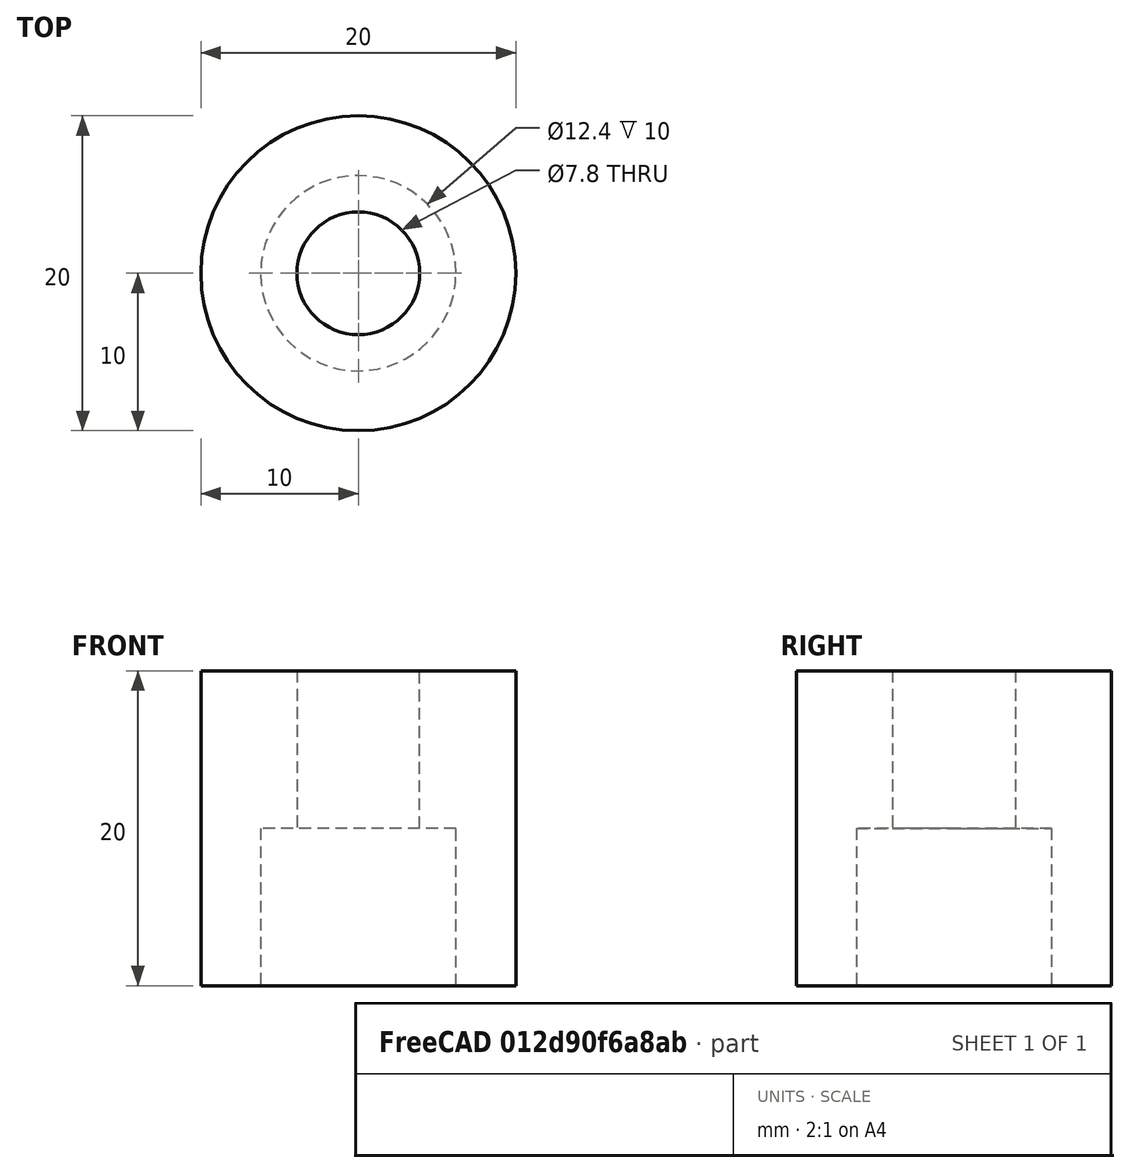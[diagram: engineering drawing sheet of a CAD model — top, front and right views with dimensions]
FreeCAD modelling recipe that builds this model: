
FCSTD DOCUMENT  (FreeCAD 1.0R38641 +468 (Git))
Label: m8_tube_extension
License: All rights reserved
LicenseURL: https://en.wikipedia.org/wiki/All_rights_reserved
objects: Sketcher::SketchObject×2, PartDesign::Pad×1, PartDesign::Pocket×1, PartDesign::Body×1
note: 11 computed .brp shape members not serialized (recipe doc carries the construction recipe); baked Part::Feature solids carry a one-line shape summary decoded from their .brp

FEATURE [Sketcher::SketchObject] Sketch
  ArcFitTolerance = 1e-06
  AttachmentSupport = -> [XY_Plane]
  FullyConstrained = false
  MakeInternals = false
  MapMode = 5
  sketch-geometry (2):
    g0: Circle CenterX=0 CenterY=0 CenterZ=0 NormalX=0 NormalY=0 NormalZ=1 AngleXU=0 Radius=10
    g1: Circle CenterX=0 CenterY=0 CenterZ=0 NormalX=0 NormalY=0 NormalZ=1 AngleXU=0 Radius=3.9
  constraints (3):
    c: Diameter(g0) = 20
    c: Diameter(g1) = 7.8
    c: Coincident(g1,g0)
FEATURE [PartDesign::Pad] Pad
  Direction = (0,0,1)
  Length = 20
  Length2 = 10
  Profile = -> Sketch
  ReferenceAxis = -> Sketch [N_Axis]
  Refine = true
  Suppressed = false
  Type = 0
FEATURE [Sketcher::SketchObject] Sketch001
  ArcFitTolerance = 1e-06
  AttachmentSupport = -> [XY_Plane]
  FullyConstrained = true
  MakeInternals = false
  MapMode = 5
  sketch-geometry (1):
    g0: Circle CenterX=0 CenterY=0 CenterZ=0 NormalX=0 NormalY=0 NormalZ=1 AngleXU=0 Radius=6.2
  constraints (2):
    c: Diameter(g0) = 12.4
    c: Coincident(g0,g-1)
FEATURE [PartDesign::Pocket] Pocket
  BaseFeature = -> Pad
  Direction = (0,0,-1)
  Length = 10
  Length2 = 5
  Profile = -> Sketch001
  ReferenceAxis = -> Sketch001 [N_Axis]
  Refine = true
  Reversed = true
  Suppressed = false
  Type = 0
FEATURE [PartDesign::Body] Body
  AllowCompound = false
  Group = -> [Sketch,Pad,Sketch001,Pocket]
  Origin = -> Origin
  Tip = -> Pocket
